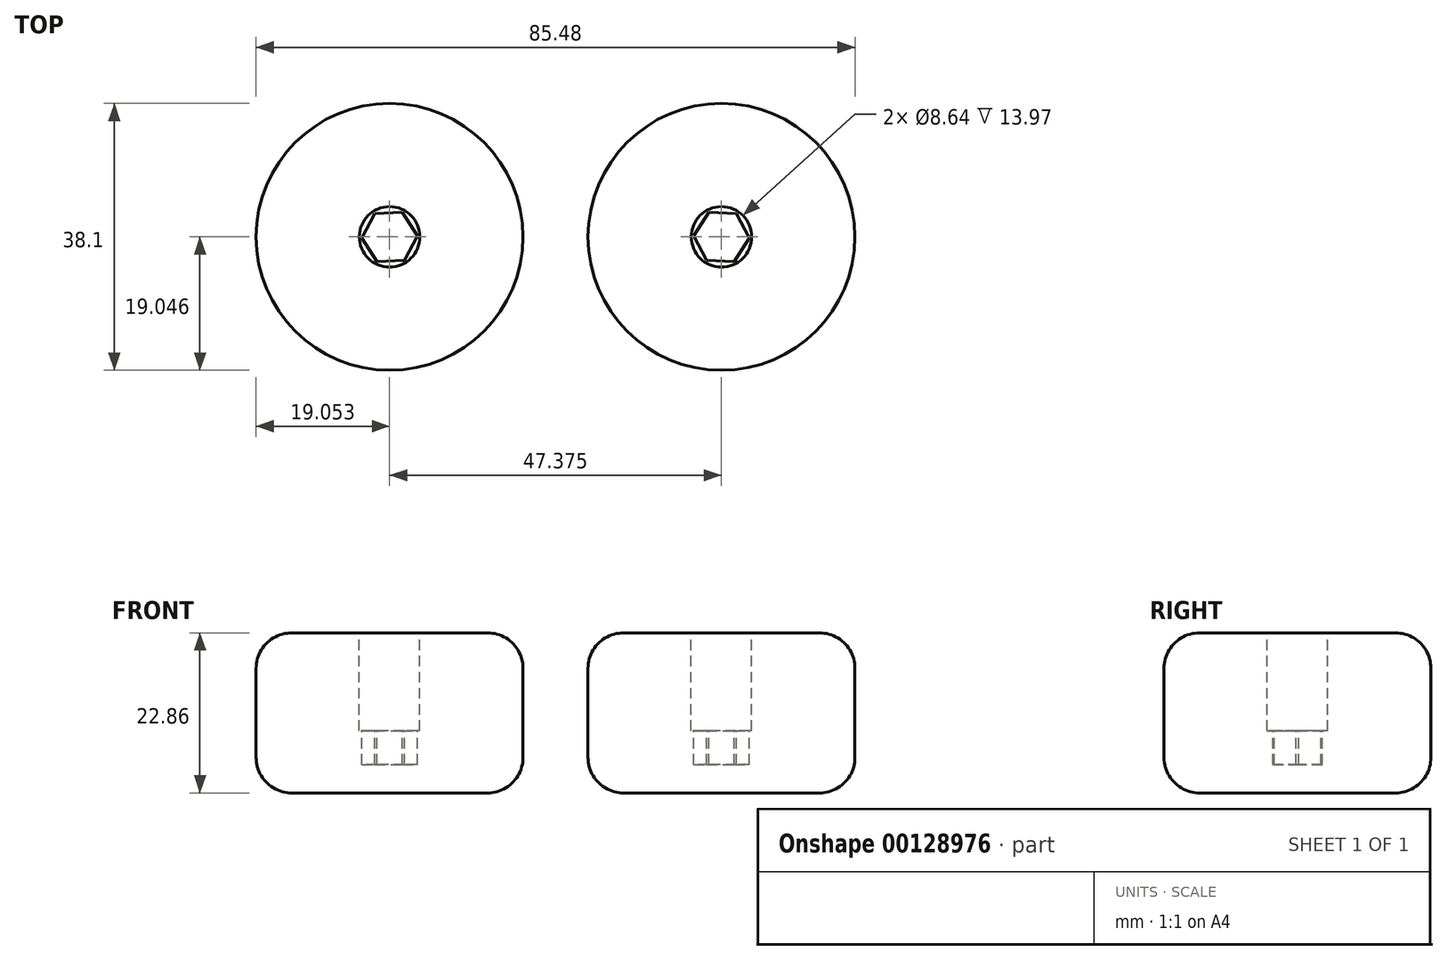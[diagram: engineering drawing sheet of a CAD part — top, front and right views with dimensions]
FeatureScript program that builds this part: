
annotation { "Feature Type Name" : "Feature", "Feature Type Description" : "" }
export const myFeature = defineFeature(function(context is Context, id is Id, definition is map)
    precondition{}
    {
        {
            var Q0;
            Q0=qCreatedBy(makeId("Top.planeOp"),FACE);
            var sketch = newSketch(context, id + "F0", { "sketchPlane" : qUnion([Q0])});
            skLineSegment(sketch, "E0", {"start": v(0, 75.14) * mm, "end": v(0, -71.6) * mm, "construction": true});
            skCircle(sketch, "E1", {"center": v(-23.69, 26.18) * mm, "radius": 19.05 * mm});
            skCircle(sketch, "E2.MirrorC", {"center": v(23.69, 26.18) * mm, "radius": 19.05 * mm});
            skSolve(sketch);
        }
        {
            var Q0;
            Q0 = qSketchRegion(id + "F0", true);
            extrude(context, id + "F1", {"entities" : qUnion([Q0]), "depth" : 22.86 * mm});
        }
        {
            var Q0;
            Q0=makeQuery(id+"F1.opExtrude","CAP_FACE",FACE,{"disambiguationData":[OSD([sQuery(id+"F0.wireOp",EDGE,"E1")])],"isStart":false});
            var sketch = newSketch(context, id + "F2", { "sketchPlane" : qUnion([Q0])});
            skCircle(sketch, "E3", {"center": v(-23.69, 26.18) * mm, "radius": 4.32 * mm});
            skLineSegment(sketch, "E4", {"start": v(0, 68.75) * mm, "end": v(0, -51.03) * mm, "construction": true});
            skCircle(sketch, "E5.MirrorC", {"center": v(23.69, 26.18) * mm, "radius": 4.32 * mm});
            skSolve(sketch);
        }
        {
            var Q0;
            Q0 = qSketchRegion(id + "F2", true);
            extrude(context, id + "F3", {"entities" : qUnion([Q0]), "operationType" : NewBodyOperationType.REMOVE, "oppositeDirection" : true, "depth" : 13.97 * mm});
        }
        {
            var Q0;
            Q0=makeQuery(id+"F3.boolean.opBoolean","COPY",FACE,{"derivedFrom":makeQuery(id+"F3.opExtrude","CAP_FACE",FACE,{"disambiguationData":[OSD([sQuery(id+"F2.wireOp",EDGE,"E3")])],"isStart":false})});
            var sketch = newSketch(context, id + "F4", { "sketchPlane" : qUnion([Q0])});
            skCircle(sketch, "E6.cCircle", {"center": v(-23.69, 26.18) * mm, "radius": 3.43 * mm, "construction": true});
            skLineSegment(sketch, "E6.0", {"start": v(-19.73, 26.36) * mm, "end": v(-21.55, 22.84) * mm});
            skLineSegment(sketch, "E6.1", {"start": v(-21.55, 22.84) * mm, "end": v(-25.51, 22.66) * mm});
            skLineSegment(sketch, "E6.2", {"start": v(-25.51, 22.66) * mm, "end": v(-27.64, 26) * mm});
            skLineSegment(sketch, "E6.3", {"start": v(-27.64, 26) * mm, "end": v(-25.82, 29.51) * mm});
            skLineSegment(sketch, "E6.4", {"start": v(-25.82, 29.51) * mm, "end": v(-21.86, 29.7) * mm});
            skLineSegment(sketch, "E6.5", {"start": v(-21.86, 29.7) * mm, "end": v(-19.73, 26.36) * mm});
            skPoint(sketch, "E6.0.midPoint", {"position": v(-20.64, 24.6) * mm});
            skLineSegment(sketch, "E7", {"start": v(0, 58.05) * mm, "end": v(0, -40.8) * mm, "construction": true});
            skCircle(sketch, "E8.MirrorC", {"center": v(23.69, 26.18) * mm, "radius": 3.43 * mm, "construction": true});
            skLineSegment(sketch, "E9.MirrorCS", {"start": v(21.86, 29.7) * mm, "end": v(19.73, 26.36) * mm});
            skLineSegment(sketch, "E10.MirrorCS", {"start": v(25.82, 29.51) * mm, "end": v(21.86, 29.7) * mm});
            skLineSegment(sketch, "E11.MirrorCS", {"start": v(27.64, 26) * mm, "end": v(25.82, 29.51) * mm});
            skLineSegment(sketch, "E12.MirrorCS", {"start": v(25.51, 22.66) * mm, "end": v(27.64, 26) * mm});
            skLineSegment(sketch, "E13.MirrorCS", {"start": v(21.55, 22.84) * mm, "end": v(25.51, 22.66) * mm});
            skLineSegment(sketch, "E14.MirrorCS", {"start": v(19.73, 26.36) * mm, "end": v(21.55, 22.84) * mm});
            skSolve(sketch);
        }
        {
            var Q0;
            Q0 = qSketchRegion(id + "F4", true);
            extrude(context, id + "F5", {"entities" : qUnion([Q0]), "operationType" : NewBodyOperationType.REMOVE, "oppositeDirection" : true, "depth" : 4.83 * mm});
        }
        {
            var Q0;
            Q0=makeQuery(id+"F1.opExtrude","CAP_FACE",FACE,{"disambiguationData":[OSD([sQuery(id+"F0.wireOp",EDGE,"E1")])],"isStart":true});
            var Q1;
            Q1=makeQuery(id+"F1.opExtrude","SWEPT_FACE",FACE,{"disambiguationData":[OSD([sQuery(id+"F0.wireOp",EDGE,"E1")])]});
            var Q2;
            Q2=makeQuery(id+"F1.opExtrude","CAP_FACE",FACE,{"disambiguationData":[OSD([sQuery(id+"F0.wireOp",EDGE,"E2.MirrorC")])],"isStart":true});
            var Q3;
            Q3=makeQuery(id+"F1.opExtrude","SWEPT_FACE",FACE,{"disambiguationData":[OSD([sQuery(id+"F0.wireOp",EDGE,"E2.MirrorC")])]});
            fillet(context, id + "F6", {"entities" : qUnion([Q0, Q1, Q2, Q3]), "radius" : 5.08 * mm, "tangentPropagation" : true, "allowEdgeOverflow" : false});
        }
    });
